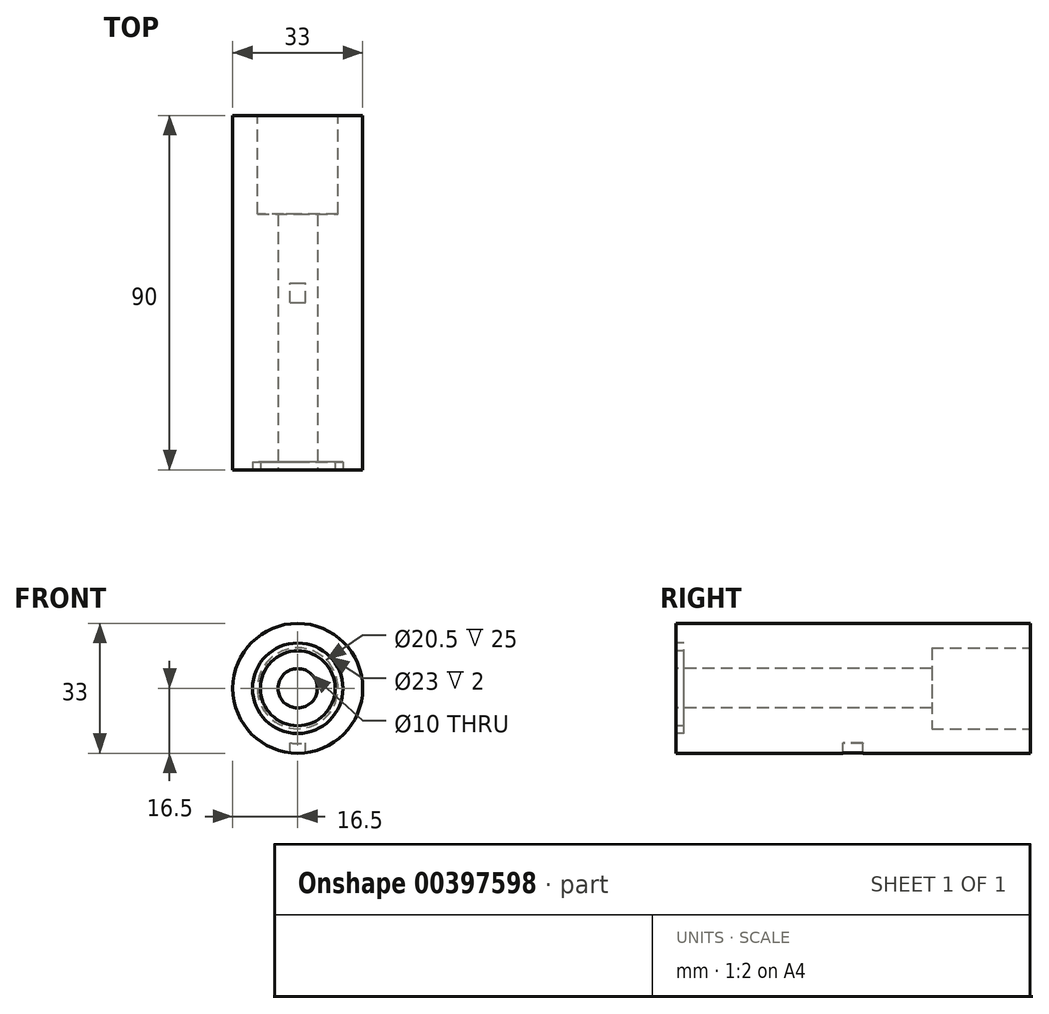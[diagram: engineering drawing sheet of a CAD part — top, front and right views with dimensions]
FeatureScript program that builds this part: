
annotation { "Feature Type Name" : "Feature", "Feature Type Description" : "" }
export const myFeature = defineFeature(function(context is Context, id is Id, definition is map)
    precondition{}
    {
        {
            var Q0;
            Q0=qCreatedBy(makeId("Front.planeOp"),FACE);
            var sketch = newSketch(context, id + "F0", { "sketchPlane" : qUnion([Q0])});
            skCircle(sketch, "E0", {"center": v(0, 0) * mm, "radius": 16.5 * mm});
            skSolve(sketch);
        }
        {
            var Q0;
            Q0=qSketchRegion(id+"F0",true);
            extrude(context, id + "F1", {"entities" : qUnion([Q0]), "depth" : 90 * mm});
        }
        {
            var Q0;
            Q0=makeQuery(id+"F1.opExtrude","CAP_FACE",FACE,{"disambiguationData":[OSD([sQuery(id+"F0.wireOp",EDGE,"E0")])],"isStart":true});
            var sketch = newSketch(context, id + "F2", { "sketchPlane" : qUnion([Q0])});
            skCircle(sketch, "E1", {"center": v(0, 0) * mm, "radius": 10.25 * mm});
            skSolve(sketch);
        }
        {
            var Q0;
            Q0=qSketchRegion(id+"F2",true);
            extrude(context, id + "F3", {"entities" : qUnion([Q0]), "operationType" : NewBodyOperationType.REMOVE, "oppositeDirection" : true, "depth" : 25 * mm});
        }
        {
            var Q0;
            Q0=makeQuery(id+"F1.opExtrude","CAP_FACE",FACE,{"disambiguationData":[OSD([sQuery(id+"F0.wireOp",EDGE,"E0")])],"isStart":false});
            var sketch = newSketch(context, id + "F4", { "sketchPlane" : qUnion([Q0])});
            skCircle(sketch, "E2", {"center": v(0, 0) * mm, "radius": 11.5 * mm});
            skSolve(sketch);
        }
        {
            var Q0;
            Q0=makeQuery(id+"F4.imprint","IMPRINT",FACE,{"disambiguationData":[TD([[makeQuery(id+"F4.imprint","IMPRINT",EDGE,{"derivedFrom":sQuery(id+"F4.wireOp",EDGE,"E2")}),-1.0]])]});
            var sketch = newSketch(context, id + "F5", { "sketchPlane" : qUnion([Q0])});
            skCircle(sketch, "E3", {"center": v(0, 0) * mm, "radius": 3.5 * mm});
            skSolve(sketch);
        }
        {
            var Q0;
            Q0=qCreatedBy(makeId("Top.planeOp"),FACE);
            var sketch = newSketch(context, id + "F6", { "sketchPlane" : qUnion([Q0])});
            skLineSegment(sketch, "E4", {"start": v(0, 0) * mm, "end": v(0, -90) * mm});
            skLineSegment(sketch, "E5.bottom", {"start": v(-2, -42.5) * mm, "end": v(2, -42.5) * mm});
            skLineSegment(sketch, "E5.top", {"start": v(-2, -47.5) * mm, "end": v(2, -47.5) * mm});
            skLineSegment(sketch, "E5.left", {"start": v(-2, -42.5) * mm, "end": v(-2, -47.5) * mm});
            skLineSegment(sketch, "E5.right", {"start": v(2, -42.5) * mm, "end": v(2, -47.5) * mm});
            skPoint(sketch, "E5.middle", {"position": v(0, -45) * mm});
            skSolve(sketch);
        }
        {
            var Q0;
            Q0=qSketchRegion(id+"F6",true);
            extrude(context, id + "F7", {"entities" : qUnion([Q0]), "operationType" : NewBodyOperationType.REMOVE, "oppositeDirection" : true, "depth" : 25 * mm});
        }
        {
            var Q0;
            Q0=makeQuery(id+"F4.imprint","IMPRINT",FACE,{"disambiguationData":[TD([[makeQuery(id+"F4.imprint","IMPRINT",EDGE,{"derivedFrom":sQuery(id+"F4.wireOp",EDGE,"E2")}),-1.0]])]});
            var sketch = newSketch(context, id + "F8", { "sketchPlane" : qUnion([Q0])});
            skCircle(sketch, "E6", {"center": v(0, 0) * mm, "radius": 14 * mm});
            skSolve(sketch);
        }
        {
            var Q0;
            Q0=qSketchRegion(id+"F8",true);
            extrude(context, id + "F9", {"entities" : qUnion([Q0]), "operationType" : NewBodyOperationType.ADD, "oppositeDirection" : true, "depth" : 53.8 * mm});
        }
        {
            var Q0;
            Q0=makeQuery(id+"F4.imprint","IMPRINT",FACE,{"disambiguationData":[TD([[makeQuery(id+"F4.imprint","IMPRINT",EDGE,{"derivedFrom":sQuery(id+"F4.wireOp",EDGE,"E2")}),-1.0]])]});
            var sketch = newSketch(context, id + "F10", { "sketchPlane" : qUnion([Q0])});
            skCircle(sketch, "E7", {"center": v(0, 0) * mm, "radius": 8.5 * mm});
            skSolve(sketch);
        }
        {
            var Q0;
            Q0=qSketchRegion(id+"F10",true);
            extrude(context, id + "F11", {"entities" : qUnion([Q0]), "operationType" : NewBodyOperationType.ADD, "oppositeDirection" : true, "depth" : 24.9 * mm});
        }
        {
            var Q0;
            Q0=makeQuery(id+"F4.imprint","IMPRINT",FACE,{"disambiguationData":[TD([[makeQuery(id+"F4.imprint","IMPRINT",EDGE,{"derivedFrom":sQuery(id+"F4.wireOp",EDGE,"E2")}),1.0]])]});
            extrude(context, id + "F12", {"entities" : qUnion([Q0]), "operationType" : NewBodyOperationType.REMOVE, "oppositeDirection" : true, "depth" : 2 * mm});
        }
        {
            var Q0;
            Q0=makeQuery(id+"F5.imprint","IMPRINT",FACE,{"disambiguationData":[TD([[makeQuery(id+"F5.imprint","IMPRINT",EDGE,{"derivedFrom":sQuery(id+"F5.wireOp",EDGE,"E3")}),-1.0]])]});
            var sketch = newSketch(context, id + "F13", { "sketchPlane" : qUnion([Q0])});
            skCircle(sketch, "E8", {"center": v(0, 0) * mm, "radius": 9.5 * mm});
            skSolve(sketch);
        }
        {
            var Q0;
            Q0=makeQuery(id+"F13.imprint","IMPRINT",FACE,{"disambiguationData":[TD([[makeQuery(id+"F13.imprint","IMPRINT",EDGE,{"derivedFrom":sQuery(id+"F13.wireOp",EDGE,"E8")}),1.0]])]});
            var Q1;
            Q1=makeQuery(id+"F5.imprint","IMPRINT",FACE,{"disambiguationData":[TD([[makeQuery(id+"F5.imprint","IMPRINT",EDGE,{"derivedFrom":sQuery(id+"F5.wireOp",EDGE,"E3")}),1.0]])]});
            extrude(context, id + "F14", {"entities" : qUnion([Q0, Q1]), "operationType" : NewBodyOperationType.ADD, "oppositeDirection" : true, "depth" : 4.1 * mm});
        }
        {
            var Q0;
            {var subQ0=sQuery(id+"F5.wireOp",EDGE,"E3");Q0=makeQuery(id+"F14.boolean.opBoolean","MERGE",FACE,{"derivedFrom":[makeQuery(id+"F14.opExtrude","CAP_FACE",FACE,{"disambiguationData":[OSD([subQ0])],"isStart":true}),makeQuery(id+"F14.opExtrude","CAP_FACE",FACE,{"disambiguationData":[OSD([subQ0,sQuery(id+"F13.wireOp",EDGE,"E8")])],"isStart":true})]});}
            var sketch = newSketch(context, id + "F15", { "sketchPlane" : qUnion([Q0])});
            skCircle(sketch, "E9", {"center": v(0, 0) * mm, "radius": 5 * mm});
            skSolve(sketch);
        }
        {
            var Q0;
            Q0=makeQuery(id+"F15.imprint","IMPRINT",FACE,{"disambiguationData":[TD([[makeQuery(id+"F15.imprint","IMPRINT",EDGE,{"derivedFrom":sQuery(id+"F15.wireOp",EDGE,"E9")}),1.0]])]});
            extrude(context, id + "F16", {"entities" : qUnion([Q0]), "operationType" : NewBodyOperationType.REMOVE, "oppositeDirection" : true, "depth" : 92.2 * mm});
        }
    });
